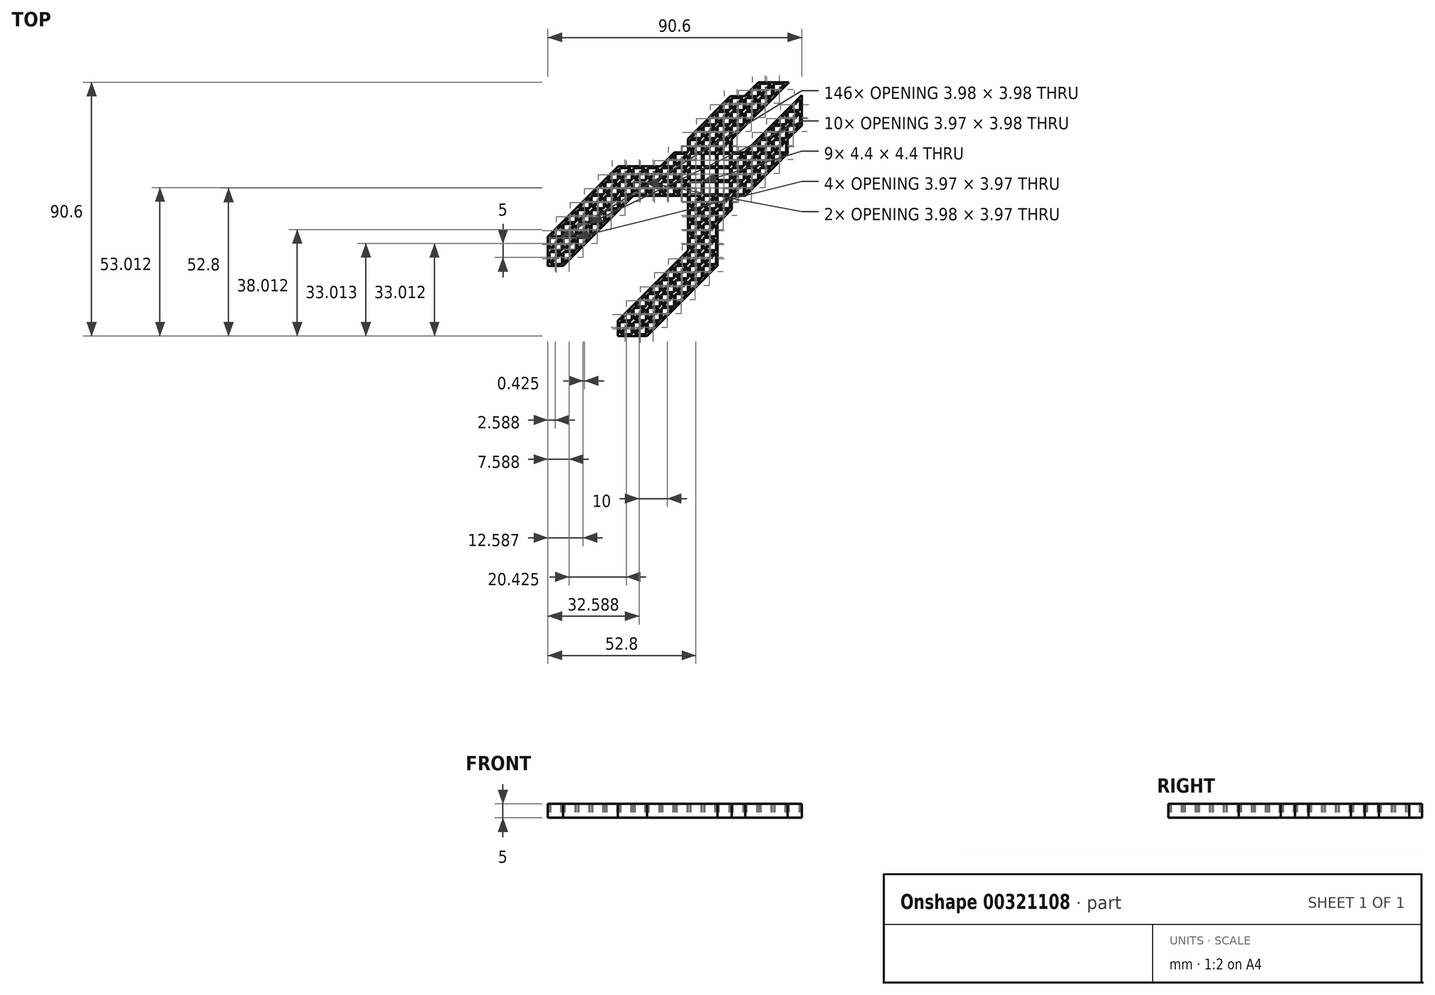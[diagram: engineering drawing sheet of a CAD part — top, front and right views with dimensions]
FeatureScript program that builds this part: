
annotation { "Feature Type Name" : "Feature", "Feature Type Description" : "" }
export const myFeature = defineFeature(function(context is Context, id is Id, definition is map)
    precondition{}
    {
        {
            var Q0;
            Q0=qCreatedBy(makeId("Top.planeOp"),FACE);
            var sketch = newSketch(context, id + "F0", { "sketchPlane" : qUnion([Q0])});
            skLineSegment(sketch, "E0", {"start": v(25.72, 10.3) * mm, "end": v(29.7, 14.28) * mm});
            skLineSegment(sketch, "E1", {"start": v(29.7, 14.28) * mm, "end": v(29.7, 10.3) * mm});
            skLineSegment(sketch, "E2", {"start": v(29.7, 10.3) * mm, "end": v(25.72, 10.3) * mm});
            skLineSegment(sketch, "E3", {"start": v(19.7, 0.3) * mm, "end": v(15.72, 0.3) * mm});
            skLineSegment(sketch, "E4", {"start": v(15.72, 0.3) * mm, "end": v(19.7, 4.28) * mm});
            skLineSegment(sketch, "E5", {"start": v(19.7, 4.28) * mm, "end": v(19.7, 0.3) * mm});
            skLineSegment(sketch, "E6", {"start": v(5.72, -24.7) * mm, "end": v(9.7, -20.72) * mm});
            skLineSegment(sketch, "E7", {"start": v(9.7, -20.72) * mm, "end": v(9.7, -24.7) * mm});
            skLineSegment(sketch, "E8", {"start": v(9.7, -24.7) * mm, "end": v(5.72, -24.7) * mm});
            skLineSegment(sketch, "E9", {"start": v(0.72, -29.7) * mm, "end": v(4.7, -25.72) * mm});
            skLineSegment(sketch, "E10", {"start": v(4.7, -25.72) * mm, "end": v(4.7, -29.7) * mm});
            skLineSegment(sketch, "E11", {"start": v(4.7, -29.7) * mm, "end": v(0.72, -29.7) * mm});
            skLineSegment(sketch, "E12", {"start": v(-4.28, -34.7) * mm, "end": v(-0.3, -30.72) * mm});
            skLineSegment(sketch, "E13", {"start": v(-0.3, -30.72) * mm, "end": v(-0.3, -34.7) * mm});
            skLineSegment(sketch, "E14", {"start": v(-0.3, -34.7) * mm, "end": v(-4.28, -34.7) * mm});
            skLineSegment(sketch, "E15", {"start": v(-9.28, -39.7) * mm, "end": v(-5.3, -35.72) * mm});
            skLineSegment(sketch, "E16", {"start": v(-5.3, -35.72) * mm, "end": v(-5.3, -39.7) * mm});
            skLineSegment(sketch, "E17", {"start": v(-5.3, -39.7) * mm, "end": v(-9.28, -39.7) * mm});
            skLineSegment(sketch, "E18", {"start": v(-19.7, -40.3) * mm, "end": v(-15.72, -40.3) * mm});
            skLineSegment(sketch, "E19", {"start": v(-15.72, -40.3) * mm, "end": v(-19.7, -44.28) * mm});
            skLineSegment(sketch, "E20", {"start": v(-19.7, -44.28) * mm, "end": v(-19.7, -40.3) * mm});
            skLineSegment(sketch, "E21", {"start": v(-24.28, 0.3) * mm, "end": v(-20.3, 4.28) * mm});
            skLineSegment(sketch, "E22", {"start": v(-20.3, 4.28) * mm, "end": v(-20.3, 0.3) * mm});
            skLineSegment(sketch, "E23", {"start": v(-20.3, 0.3) * mm, "end": v(-24.28, 0.3) * mm});
            skLineSegment(sketch, "E24", {"start": v(-29.28, -4.7) * mm, "end": v(-25.3, -0.72) * mm});
            skLineSegment(sketch, "E25", {"start": v(-25.3, -0.72) * mm, "end": v(-25.3, -4.7) * mm});
            skLineSegment(sketch, "E26", {"start": v(-25.3, -4.7) * mm, "end": v(-29.28, -4.7) * mm});
            skLineSegment(sketch, "E27", {"start": v(-39.28, -14.7) * mm, "end": v(-35.3, -10.72) * mm});
            skLineSegment(sketch, "E28", {"start": v(-35.3, -10.72) * mm, "end": v(-35.3, -14.7) * mm});
            skLineSegment(sketch, "E29", {"start": v(-35.3, -14.7) * mm, "end": v(-39.28, -14.7) * mm});
            skLineSegment(sketch, "E30", {"start": v(34.7, 40.3) * mm, "end": v(30.72, 40.3) * mm});
            skLineSegment(sketch, "E31", {"start": v(30.72, 40.3) * mm, "end": v(34.7, 44.28) * mm});
            skLineSegment(sketch, "E32", {"start": v(34.7, 44.28) * mm, "end": v(34.7, 40.3) * mm});
            skLineSegment(sketch, "E33", {"start": v(25.72, 35.3) * mm, "end": v(29.7, 39.28) * mm});
            skLineSegment(sketch, "E34", {"start": v(29.7, 39.28) * mm, "end": v(29.7, 35.3) * mm});
            skLineSegment(sketch, "E35", {"start": v(29.7, 35.3) * mm, "end": v(25.72, 35.3) * mm});
            skLineSegment(sketch, "E36", {"start": v(20.72, 30.3) * mm, "end": v(24.7, 34.28) * mm});
            skLineSegment(sketch, "E37", {"start": v(24.7, 34.28) * mm, "end": v(24.7, 30.3) * mm});
            skLineSegment(sketch, "E38", {"start": v(24.7, 30.3) * mm, "end": v(20.72, 30.3) * mm});
            skLineSegment(sketch, "E39", {"start": v(-15.3, 9.28) * mm, "end": v(-15.3, 5.3) * mm});
            skLineSegment(sketch, "E40", {"start": v(-15.3, 5.3) * mm, "end": v(-19.28, 5.3) * mm});
            skLineSegment(sketch, "E41", {"start": v(-19.28, 5.3) * mm, "end": v(-15.3, 9.28) * mm});
            skLineSegment(sketch, "E42", {"start": v(-19.7, 5.72) * mm, "end": v(-19.7, 9.7) * mm});
            skLineSegment(sketch, "E43", {"start": v(-19.7, 9.7) * mm, "end": v(-15.72, 9.7) * mm});
            skLineSegment(sketch, "E44", {"start": v(-15.72, 9.7) * mm, "end": v(-19.7, 5.72) * mm});
            skLineSegment(sketch, "E45", {"start": v(-15.3, 10.3) * mm, "end": v(-19.28, 10.3) * mm});
            skLineSegment(sketch, "E46", {"start": v(-19.28, 10.3) * mm, "end": v(-15.3, 14.28) * mm});
            skLineSegment(sketch, "E47", {"start": v(-15.3, 14.28) * mm, "end": v(-15.3, 10.3) * mm});
            skLineSegment(sketch, "E48", {"start": v(-20.3, 5.3) * mm, "end": v(-24.28, 5.3) * mm});
            skLineSegment(sketch, "E49", {"start": v(-24.28, 5.3) * mm, "end": v(-20.3, 9.28) * mm});
            skLineSegment(sketch, "E50", {"start": v(-20.3, 9.28) * mm, "end": v(-20.3, 5.3) * mm});
            skLineSegment(sketch, "E51", {"start": v(-34.28, -4.7) * mm, "end": v(-30.3, -0.72) * mm});
            skLineSegment(sketch, "E52", {"start": v(-30.3, -0.72) * mm, "end": v(-30.3, -4.7) * mm});
            skLineSegment(sketch, "E53", {"start": v(-30.3, -4.7) * mm, "end": v(-34.28, -4.7) * mm});
            skLineSegment(sketch, "E54", {"start": v(-39.28, -9.7) * mm, "end": v(-35.3, -5.72) * mm});
            skLineSegment(sketch, "E55", {"start": v(-35.3, -5.72) * mm, "end": v(-35.3, -9.7) * mm});
            skLineSegment(sketch, "E56", {"start": v(-35.3, -9.7) * mm, "end": v(-39.28, -9.7) * mm});
            skLineSegment(sketch, "E57", {"start": v(-40.3, -14.7) * mm, "end": v(-44.28, -14.7) * mm});
            skLineSegment(sketch, "E58", {"start": v(-44.28, -14.7) * mm, "end": v(-40.3, -10.72) * mm});
            skLineSegment(sketch, "E59", {"start": v(-40.3, -10.72) * mm, "end": v(-40.3, -14.7) * mm});
            skLineSegment(sketch, "E60", {"start": v(-39.7, -10.3) * mm, "end": v(-35.72, -10.3) * mm});
            skLineSegment(sketch, "E61", {"start": v(-35.72, -10.3) * mm, "end": v(-39.7, -14.27) * mm});
            skLineSegment(sketch, "E62", {"start": v(-39.7, -14.27) * mm, "end": v(-39.7, -10.3) * mm});
            skLineSegment(sketch, "E63", {"start": v(-34.7, -5.3) * mm, "end": v(-30.72, -5.3) * mm});
            skLineSegment(sketch, "E64", {"start": v(-30.72, -5.3) * mm, "end": v(-34.7, -9.28) * mm});
            skLineSegment(sketch, "E65", {"start": v(-34.7, -9.28) * mm, "end": v(-34.7, -5.3) * mm});
            skLineSegment(sketch, "E66", {"start": v(-29.7, -0.3) * mm, "end": v(-25.72, -0.3) * mm});
            skLineSegment(sketch, "E67", {"start": v(-25.72, -0.3) * mm, "end": v(-29.7, -4.28) * mm});
            skLineSegment(sketch, "E68", {"start": v(-29.7, -4.28) * mm, "end": v(-29.7, -0.3) * mm});
            skLineSegment(sketch, "E69", {"start": v(-29.28, 0.3) * mm, "end": v(-25.3, 4.28) * mm});
            skLineSegment(sketch, "E70", {"start": v(-25.3, 4.28) * mm, "end": v(-25.3, 0.3) * mm});
            skLineSegment(sketch, "E71", {"start": v(-25.3, 0.3) * mm, "end": v(-29.28, 0.3) * mm});
            skLineSegment(sketch, "E72", {"start": v(-24.7, 4.7) * mm, "end": v(-20.72, 4.7) * mm});
            skLineSegment(sketch, "E73", {"start": v(-20.72, 4.7) * mm, "end": v(-24.7, 0.72) * mm});
            skLineSegment(sketch, "E74", {"start": v(-24.7, 0.72) * mm, "end": v(-24.7, 4.7) * mm});
            skLineSegment(sketch, "E75", {"start": v(-14.7, 9.7) * mm, "end": v(-10.72, 9.7) * mm});
            skLineSegment(sketch, "E76", {"start": v(-10.72, 9.7) * mm, "end": v(-14.7, 5.72) * mm});
            skLineSegment(sketch, "E77", {"start": v(-14.7, 5.72) * mm, "end": v(-14.7, 9.7) * mm});
            skLineSegment(sketch, "E78", {"start": v(34.7, 19.28) * mm, "end": v(34.7, 15.3) * mm});
            skLineSegment(sketch, "E79", {"start": v(34.7, 15.3) * mm, "end": v(30.72, 15.3) * mm});
            skLineSegment(sketch, "E80", {"start": v(30.72, 15.3) * mm, "end": v(34.7, 19.28) * mm});
            skLineSegment(sketch, "E81", {"start": v(30.3, 15.72) * mm, "end": v(30.3, 19.7) * mm});
            skLineSegment(sketch, "E82", {"start": v(30.3, 19.7) * mm, "end": v(34.28, 19.7) * mm});
            skLineSegment(sketch, "E83", {"start": v(34.28, 19.7) * mm, "end": v(30.3, 15.72) * mm});
            skLineSegment(sketch, "E84", {"start": v(30.72, 20.3) * mm, "end": v(34.7, 24.28) * mm});
            skLineSegment(sketch, "E85", {"start": v(34.7, 24.28) * mm, "end": v(34.7, 20.3) * mm});
            skLineSegment(sketch, "E86", {"start": v(34.7, 20.3) * mm, "end": v(30.72, 20.3) * mm});
            skLineSegment(sketch, "E87", {"start": v(29.7, 15.3) * mm, "end": v(25.72, 15.3) * mm});
            skLineSegment(sketch, "E88", {"start": v(25.72, 15.3) * mm, "end": v(29.7, 19.28) * mm});
            skLineSegment(sketch, "E89", {"start": v(29.7, 19.28) * mm, "end": v(29.7, 15.3) * mm});
            skLineSegment(sketch, "E90", {"start": v(5.3, 19.7) * mm, "end": v(9.7, 19.7) * mm});
            skLineSegment(sketch, "E91", {"start": v(9.7, 19.7) * mm, "end": v(9.7, 15.3) * mm});
            skLineSegment(sketch, "E92", {"start": v(9.7, 15.3) * mm, "end": v(5.3, 15.3) * mm});
            skLineSegment(sketch, "E93", {"start": v(5.3, 15.3) * mm, "end": v(5.3, 19.7) * mm});
            skLineSegment(sketch, "E94", {"start": v(20.3, 14.7) * mm, "end": v(24.28, 14.7) * mm});
            skLineSegment(sketch, "E95", {"start": v(24.28, 14.7) * mm, "end": v(20.3, 10.72) * mm});
            skLineSegment(sketch, "E96", {"start": v(20.3, 10.72) * mm, "end": v(20.3, 14.7) * mm});
            skLineSegment(sketch, "E97", {"start": v(19.7, 10.3) * mm, "end": v(15.3, 10.3) * mm});
            skLineSegment(sketch, "E98", {"start": v(15.3, 10.3) * mm, "end": v(15.3, 14.7) * mm});
            skLineSegment(sketch, "E99", {"start": v(15.3, 14.7) * mm, "end": v(19.7, 14.7) * mm});
            skLineSegment(sketch, "E100", {"start": v(19.7, 14.7) * mm, "end": v(19.7, 10.3) * mm});
            skLineSegment(sketch, "E101", {"start": v(10.3, 14.7) * mm, "end": v(14.7, 14.7) * mm});
            skLineSegment(sketch, "E102", {"start": v(14.7, 14.7) * mm, "end": v(14.7, 10.3) * mm});
            skLineSegment(sketch, "E103", {"start": v(14.7, 10.3) * mm, "end": v(10.3, 10.3) * mm});
            skLineSegment(sketch, "E104", {"start": v(10.3, 10.3) * mm, "end": v(10.3, 14.7) * mm});
            skLineSegment(sketch, "E105", {"start": v(14.7, 15.3) * mm, "end": v(10.3, 15.3) * mm});
            skLineSegment(sketch, "E106", {"start": v(10.3, 15.3) * mm, "end": v(10.3, 19.7) * mm});
            skLineSegment(sketch, "E107", {"start": v(10.3, 19.7) * mm, "end": v(14.7, 19.7) * mm});
            skLineSegment(sketch, "E108", {"start": v(14.7, 19.7) * mm, "end": v(14.7, 15.3) * mm});
            skLineSegment(sketch, "E109", {"start": v(14.7, 9.7) * mm, "end": v(14.7, 5.3) * mm});
            skLineSegment(sketch, "E110", {"start": v(14.7, 5.3) * mm, "end": v(10.3, 5.3) * mm});
            skLineSegment(sketch, "E111", {"start": v(10.3, 5.3) * mm, "end": v(10.3, 9.7) * mm});
            skLineSegment(sketch, "E112", {"start": v(10.3, 9.7) * mm, "end": v(14.7, 9.7) * mm});
            skLineSegment(sketch, "E113", {"start": v(10.72, 20.3) * mm, "end": v(14.7, 24.28) * mm});
            skLineSegment(sketch, "E114", {"start": v(14.7, 24.28) * mm, "end": v(14.7, 20.3) * mm});
            skLineSegment(sketch, "E115", {"start": v(14.7, 20.3) * mm, "end": v(10.72, 20.3) * mm});
            skLineSegment(sketch, "E116", {"start": v(10.72, 25.3) * mm, "end": v(14.7, 29.28) * mm});
            skLineSegment(sketch, "E117", {"start": v(14.7, 29.28) * mm, "end": v(14.7, 25.3) * mm});
            skLineSegment(sketch, "E118", {"start": v(14.7, 25.3) * mm, "end": v(10.72, 25.3) * mm});
            skLineSegment(sketch, "E119", {"start": v(15.3, 29.7) * mm, "end": v(19.28, 29.7) * mm});
            skLineSegment(sketch, "E120", {"start": v(19.28, 29.7) * mm, "end": v(15.3, 25.72) * mm});
            skLineSegment(sketch, "E121", {"start": v(15.3, 25.72) * mm, "end": v(15.3, 29.7) * mm});
            skLineSegment(sketch, "E122", {"start": v(10.3, 25.73) * mm, "end": v(10.3, 29.7) * mm});
            skLineSegment(sketch, "E123", {"start": v(10.3, 29.7) * mm, "end": v(14.28, 29.7) * mm});
            skLineSegment(sketch, "E124", {"start": v(14.28, 29.7) * mm, "end": v(10.3, 25.73) * mm});
            skLineSegment(sketch, "E125", {"start": v(14.28, 24.7) * mm, "end": v(10.3, 20.72) * mm});
            skLineSegment(sketch, "E126", {"start": v(10.3, 20.72) * mm, "end": v(10.3, 24.7) * mm});
            skLineSegment(sketch, "E127", {"start": v(10.3, 24.7) * mm, "end": v(14.28, 24.7) * mm});
            skLineSegment(sketch, "E128", {"start": v(5.3, 14.7) * mm, "end": v(9.7, 14.7) * mm});
            skLineSegment(sketch, "E129", {"start": v(9.7, 14.7) * mm, "end": v(9.7, 10.3) * mm});
            skLineSegment(sketch, "E130", {"start": v(9.7, 10.3) * mm, "end": v(5.3, 10.3) * mm});
            skLineSegment(sketch, "E131", {"start": v(5.3, 10.3) * mm, "end": v(5.3, 14.7) * mm});
            skLineSegment(sketch, "E132", {"start": v(14.28, 4.7) * mm, "end": v(10.3, 0.72) * mm});
            skLineSegment(sketch, "E133", {"start": v(10.3, 0.72) * mm, "end": v(10.3, 4.7) * mm});
            skLineSegment(sketch, "E134", {"start": v(10.3, 4.7) * mm, "end": v(14.28, 4.7) * mm});
            skLineSegment(sketch, "E135", {"start": v(5.72, -4.7) * mm, "end": v(9.7, -0.72) * mm});
            skLineSegment(sketch, "E136", {"start": v(9.7, -0.72) * mm, "end": v(9.7, -4.7) * mm});
            skLineSegment(sketch, "E137", {"start": v(9.7, -4.7) * mm, "end": v(5.72, -4.7) * mm});
            skLineSegment(sketch, "E138", {"start": v(5.72, -9.7) * mm, "end": v(9.7, -5.72) * mm});
            skLineSegment(sketch, "E139", {"start": v(9.7, -5.72) * mm, "end": v(9.7, -9.7) * mm});
            skLineSegment(sketch, "E140", {"start": v(9.7, -9.7) * mm, "end": v(5.72, -9.7) * mm});
            skLineSegment(sketch, "E141", {"start": v(14.28, -10.3) * mm, "end": v(10.3, -14.28) * mm});
            skLineSegment(sketch, "E142", {"start": v(10.3, -14.28) * mm, "end": v(10.3, -10.3) * mm});
            skLineSegment(sketch, "E143", {"start": v(10.3, -10.3) * mm, "end": v(14.28, -10.3) * mm});
            skLineSegment(sketch, "E144", {"start": v(10.3, -5.3) * mm, "end": v(14.28, -5.3) * mm});
            skLineSegment(sketch, "E145", {"start": v(14.28, -5.3) * mm, "end": v(10.3, -9.28) * mm});
            skLineSegment(sketch, "E146", {"start": v(10.3, -9.28) * mm, "end": v(10.3, -5.3) * mm});
            skLineSegment(sketch, "E147", {"start": v(10.3, -0.3) * mm, "end": v(14.28, -0.3) * mm});
            skLineSegment(sketch, "E148", {"start": v(14.28, -0.3) * mm, "end": v(10.3, -4.28) * mm});
            skLineSegment(sketch, "E149", {"start": v(10.3, -4.28) * mm, "end": v(10.3, -0.3) * mm});
            skLineSegment(sketch, "E150", {"start": v(10.72, 0.3) * mm, "end": v(14.7, 4.28) * mm});
            skLineSegment(sketch, "E151", {"start": v(14.7, 4.28) * mm, "end": v(14.7, 0.3) * mm});
            skLineSegment(sketch, "E152", {"start": v(14.7, 0.3) * mm, "end": v(10.72, 0.3) * mm});
            skLineSegment(sketch, "E153", {"start": v(19.7, 5.3) * mm, "end": v(15.3, 5.3) * mm});
            skLineSegment(sketch, "E154", {"start": v(15.3, 5.3) * mm, "end": v(15.3, 9.7) * mm});
            skLineSegment(sketch, "E155", {"start": v(15.3, 9.7) * mm, "end": v(19.7, 9.7) * mm});
            skLineSegment(sketch, "E156", {"start": v(19.7, 9.7) * mm, "end": v(19.7, 5.3) * mm});
            skLineSegment(sketch, "E157", {"start": v(20.72, 10.3) * mm, "end": v(24.7, 14.28) * mm});
            skLineSegment(sketch, "E158", {"start": v(24.7, 14.28) * mm, "end": v(24.7, 10.3) * mm});
            skLineSegment(sketch, "E159", {"start": v(24.7, 10.3) * mm, "end": v(20.72, 10.3) * mm});
            skLineSegment(sketch, "E160", {"start": v(20.72, 15.3) * mm, "end": v(24.7, 19.28) * mm});
            skLineSegment(sketch, "E161", {"start": v(24.7, 19.28) * mm, "end": v(24.7, 15.3) * mm});
            skLineSegment(sketch, "E162", {"start": v(24.7, 15.3) * mm, "end": v(20.72, 15.3) * mm});
            skLineSegment(sketch, "E163", {"start": v(19.7, 15.3) * mm, "end": v(15.3, 15.3) * mm});
            skLineSegment(sketch, "E164", {"start": v(15.3, 15.3) * mm, "end": v(15.3, 19.7) * mm});
            skLineSegment(sketch, "E165", {"start": v(15.3, 19.7) * mm, "end": v(19.7, 19.7) * mm});
            skLineSegment(sketch, "E166", {"start": v(19.7, 19.7) * mm, "end": v(19.7, 15.3) * mm});
            skLineSegment(sketch, "E167", {"start": v(15.3, 24.7) * mm, "end": v(19.28, 24.7) * mm});
            skLineSegment(sketch, "E168", {"start": v(19.28, 24.7) * mm, "end": v(15.3, 20.72) * mm});
            skLineSegment(sketch, "E169", {"start": v(15.3, 20.72) * mm, "end": v(15.3, 24.7) * mm});
            skLineSegment(sketch, "E170", {"start": v(19.7, 25.3) * mm, "end": v(15.72, 25.3) * mm});
            skLineSegment(sketch, "E171", {"start": v(15.72, 25.3) * mm, "end": v(19.7, 29.28) * mm});
            skLineSegment(sketch, "E172", {"start": v(19.7, 29.28) * mm, "end": v(19.7, 25.3) * mm});
            skLineSegment(sketch, "E173", {"start": v(20.72, 35.3) * mm, "end": v(24.7, 39.28) * mm});
            skLineSegment(sketch, "E174", {"start": v(24.7, 39.28) * mm, "end": v(24.7, 35.3) * mm});
            skLineSegment(sketch, "E175", {"start": v(24.7, 35.3) * mm, "end": v(20.72, 35.3) * mm});
            skLineSegment(sketch, "E176", {"start": v(24.28, 34.7) * mm, "end": v(20.3, 30.72) * mm});
            skLineSegment(sketch, "E177", {"start": v(20.3, 30.72) * mm, "end": v(20.3, 34.7) * mm});
            skLineSegment(sketch, "E178", {"start": v(20.3, 34.7) * mm, "end": v(24.28, 34.7) * mm});
            skLineSegment(sketch, "E179", {"start": v(19.7, 30.3) * mm, "end": v(15.72, 30.3) * mm});
            skLineSegment(sketch, "E180", {"start": v(15.72, 30.3) * mm, "end": v(19.7, 34.28) * mm});
            skLineSegment(sketch, "E181", {"start": v(19.7, 34.28) * mm, "end": v(19.7, 30.3) * mm});
            skLineSegment(sketch, "E182", {"start": v(9.7, 20.3) * mm, "end": v(5.72, 20.3) * mm});
            skLineSegment(sketch, "E183", {"start": v(5.72, 20.3) * mm, "end": v(9.7, 24.28) * mm});
            skLineSegment(sketch, "E184", {"start": v(9.7, 24.28) * mm, "end": v(9.7, 20.3) * mm});
            skLineSegment(sketch, "E185", {"start": v(4.7, 15.3) * mm, "end": v(0.72, 15.3) * mm});
            skLineSegment(sketch, "E186", {"start": v(0.72, 15.3) * mm, "end": v(4.7, 19.28) * mm});
            skLineSegment(sketch, "E187", {"start": v(4.7, 19.28) * mm, "end": v(4.7, 15.3) * mm});
            skLineSegment(sketch, "E188", {"start": v(4.28, 14.7) * mm, "end": v(0.3, 10.72) * mm});
            skLineSegment(sketch, "E189", {"start": v(0.3, 10.72) * mm, "end": v(0.3, 14.7) * mm});
            skLineSegment(sketch, "E190", {"start": v(0.3, 14.7) * mm, "end": v(4.28, 14.7) * mm});
            skLineSegment(sketch, "E191", {"start": v(-0.3, 10.3) * mm, "end": v(-4.28, 10.3) * mm});
            skLineSegment(sketch, "E192", {"start": v(-4.28, 10.3) * mm, "end": v(-0.3, 14.28) * mm});
            skLineSegment(sketch, "E193", {"start": v(-0.3, 14.28) * mm, "end": v(-0.3, 10.3) * mm});
            skLineSegment(sketch, "E194", {"start": v(-5.3, 10.3) * mm, "end": v(-9.28, 10.3) * mm});
            skLineSegment(sketch, "E195", {"start": v(-9.28, 10.3) * mm, "end": v(-5.3, 14.28) * mm});
            skLineSegment(sketch, "E196", {"start": v(-5.3, 14.28) * mm, "end": v(-5.3, 10.3) * mm});
            skLineSegment(sketch, "E197", {"start": v(-4.7, 9.7) * mm, "end": v(-0.72, 9.7) * mm});
            skLineSegment(sketch, "E198", {"start": v(-0.72, 9.7) * mm, "end": v(-4.7, 5.72) * mm});
            skLineSegment(sketch, "E199", {"start": v(-4.7, 5.72) * mm, "end": v(-4.7, 9.7) * mm});
            skLineSegment(sketch, "E200", {"start": v(4.7, 14.28) * mm, "end": v(4.7, 10.3) * mm});
            skLineSegment(sketch, "E201", {"start": v(4.7, 10.3) * mm, "end": v(0.72, 10.3) * mm});
            skLineSegment(sketch, "E202", {"start": v(0.72, 10.3) * mm, "end": v(4.7, 14.28) * mm});
            skLineSegment(sketch, "E203", {"start": v(5.3, 9.7) * mm, "end": v(9.7, 9.7) * mm});
            skLineSegment(sketch, "E204", {"start": v(9.7, 9.7) * mm, "end": v(9.7, 5.3) * mm});
            skLineSegment(sketch, "E205", {"start": v(9.7, 5.3) * mm, "end": v(5.3, 5.3) * mm});
            skLineSegment(sketch, "E206", {"start": v(5.3, 5.3) * mm, "end": v(5.3, 9.7) * mm});
            skLineSegment(sketch, "E207", {"start": v(9.7, 0.3) * mm, "end": v(5.72, 0.3) * mm});
            skLineSegment(sketch, "E208", {"start": v(5.72, 0.3) * mm, "end": v(9.7, 4.28) * mm});
            skLineSegment(sketch, "E209", {"start": v(9.7, 4.28) * mm, "end": v(9.7, 0.3) * mm});
            skLineSegment(sketch, "E210", {"start": v(5.3, -0.3) * mm, "end": v(9.28, -0.3) * mm});
            skLineSegment(sketch, "E211", {"start": v(9.28, -0.3) * mm, "end": v(5.3, -4.28) * mm});
            skLineSegment(sketch, "E212", {"start": v(5.3, -4.28) * mm, "end": v(5.3, -0.3) * mm});
            skLineSegment(sketch, "E213", {"start": v(5.3, -5.3) * mm, "end": v(9.27, -5.3) * mm});
            skLineSegment(sketch, "E214", {"start": v(9.27, -5.3) * mm, "end": v(5.3, -9.28) * mm});
            skLineSegment(sketch, "E215", {"start": v(5.3, -9.28) * mm, "end": v(5.3, -5.3) * mm});
            skLineSegment(sketch, "E216", {"start": v(9.7, -14.7) * mm, "end": v(5.72, -14.7) * mm});
            skLineSegment(sketch, "E217", {"start": v(5.72, -14.7) * mm, "end": v(9.7, -10.72) * mm});
            skLineSegment(sketch, "E218", {"start": v(9.7, -10.72) * mm, "end": v(9.7, -14.7) * mm});
            skLineSegment(sketch, "E219", {"start": v(5.3, -15.3) * mm, "end": v(9.28, -15.3) * mm});
            skLineSegment(sketch, "E220", {"start": v(9.28, -15.3) * mm, "end": v(5.3, -19.28) * mm});
            skLineSegment(sketch, "E221", {"start": v(5.3, -19.28) * mm, "end": v(5.3, -15.3) * mm});
            skLineSegment(sketch, "E222", {"start": v(9.7, -15.72) * mm, "end": v(9.7, -19.7) * mm});
            skLineSegment(sketch, "E223", {"start": v(9.7, -19.7) * mm, "end": v(5.72, -19.7) * mm});
            skLineSegment(sketch, "E224", {"start": v(5.72, -19.7) * mm, "end": v(9.7, -15.72) * mm});
            skLineSegment(sketch, "E225", {"start": v(-14.28, -39.7) * mm, "end": v(-10.3, -35.72) * mm});
            skLineSegment(sketch, "E226", {"start": v(-10.3, -35.72) * mm, "end": v(-10.3, -39.7) * mm});
            skLineSegment(sketch, "E227", {"start": v(-10.3, -39.7) * mm, "end": v(-14.28, -39.7) * mm});
            skLineSegment(sketch, "E228", {"start": v(-9.7, -35.3) * mm, "end": v(-5.72, -35.3) * mm});
            skLineSegment(sketch, "E229", {"start": v(-5.72, -35.3) * mm, "end": v(-9.7, -39.28) * mm});
            skLineSegment(sketch, "E230", {"start": v(-9.7, -39.28) * mm, "end": v(-9.7, -35.3) * mm});
            skLineSegment(sketch, "E231", {"start": v(-9.28, -34.7) * mm, "end": v(-5.3, -30.72) * mm});
            skLineSegment(sketch, "E232", {"start": v(-5.3, -30.72) * mm, "end": v(-5.3, -34.7) * mm});
            skLineSegment(sketch, "E233", {"start": v(-5.3, -34.7) * mm, "end": v(-9.28, -34.7) * mm});
            skLineSegment(sketch, "E234", {"start": v(-4.7, -30.3) * mm, "end": v(-0.72, -30.3) * mm});
            skLineSegment(sketch, "E235", {"start": v(-0.72, -30.3) * mm, "end": v(-4.7, -34.28) * mm});
            skLineSegment(sketch, "E236", {"start": v(-4.7, -34.28) * mm, "end": v(-4.7, -30.3) * mm});
            skLineSegment(sketch, "E237", {"start": v(-4.28, -29.7) * mm, "end": v(-0.3, -25.72) * mm});
            skLineSegment(sketch, "E238", {"start": v(-0.3, -25.72) * mm, "end": v(-0.3, -29.7) * mm});
            skLineSegment(sketch, "E239", {"start": v(-0.3, -29.7) * mm, "end": v(-4.28, -29.7) * mm});
            skLineSegment(sketch, "E240", {"start": v(0.3, -25.3) * mm, "end": v(4.28, -25.3) * mm});
            skLineSegment(sketch, "E241", {"start": v(4.28, -25.3) * mm, "end": v(0.3, -29.28) * mm});
            skLineSegment(sketch, "E242", {"start": v(0.3, -29.28) * mm, "end": v(0.3, -25.3) * mm});
            skLineSegment(sketch, "E243", {"start": v(0.72, -24.7) * mm, "end": v(4.7, -20.72) * mm});
            skLineSegment(sketch, "E244", {"start": v(4.7, -20.72) * mm, "end": v(4.7, -24.7) * mm});
            skLineSegment(sketch, "E245", {"start": v(4.7, -24.7) * mm, "end": v(0.72, -24.7) * mm});
            skLineSegment(sketch, "E246", {"start": v(5.3, -20.3) * mm, "end": v(9.28, -20.3) * mm});
            skLineSegment(sketch, "E247", {"start": v(9.28, -20.3) * mm, "end": v(5.3, -24.28) * mm});
            skLineSegment(sketch, "E248", {"start": v(5.3, -24.28) * mm, "end": v(5.3, -20.3) * mm});
            skLineSegment(sketch, "E249", {"start": v(10.3, -15.3) * mm, "end": v(14.28, -15.3) * mm});
            skLineSegment(sketch, "E250", {"start": v(14.28, -15.3) * mm, "end": v(10.3, -19.28) * mm});
            skLineSegment(sketch, "E251", {"start": v(10.3, -19.28) * mm, "end": v(10.3, -15.3) * mm});
            skLineSegment(sketch, "E252", {"start": v(14.7, -14.7) * mm, "end": v(10.72, -14.7) * mm});
            skLineSegment(sketch, "E253", {"start": v(10.72, -14.7) * mm, "end": v(14.7, -10.72) * mm});
            skLineSegment(sketch, "E254", {"start": v(14.7, -10.72) * mm, "end": v(14.7, -14.7) * mm});
            skLineSegment(sketch, "E255", {"start": v(14.7, -9.7) * mm, "end": v(10.72, -9.7) * mm});
            skLineSegment(sketch, "E256", {"start": v(10.72, -9.7) * mm, "end": v(14.7, -5.72) * mm});
            skLineSegment(sketch, "E257", {"start": v(14.7, -5.72) * mm, "end": v(14.7, -9.7) * mm});
            skLineSegment(sketch, "E258", {"start": v(14.7, -4.7) * mm, "end": v(10.72, -4.7) * mm});
            skLineSegment(sketch, "E259", {"start": v(10.72, -4.7) * mm, "end": v(14.7, -0.72) * mm});
            skLineSegment(sketch, "E260", {"start": v(14.7, -0.72) * mm, "end": v(14.7, -4.7) * mm});
            skLineSegment(sketch, "E261", {"start": v(15.3, 4.7) * mm, "end": v(19.28, 4.7) * mm});
            skLineSegment(sketch, "E262", {"start": v(19.28, 4.7) * mm, "end": v(15.3, 0.72) * mm});
            skLineSegment(sketch, "E263", {"start": v(15.3, 0.72) * mm, "end": v(15.3, 4.7) * mm});
            skLineSegment(sketch, "E264", {"start": v(25.3, 14.7) * mm, "end": v(29.28, 14.7) * mm});
            skLineSegment(sketch, "E265", {"start": v(29.28, 14.7) * mm, "end": v(25.3, 10.72) * mm});
            skLineSegment(sketch, "E266", {"start": v(25.3, 10.72) * mm, "end": v(25.3, 14.7) * mm});
            skLineSegment(sketch, "E267", {"start": v(35.3, 24.7) * mm, "end": v(39.28, 24.7) * mm});
            skLineSegment(sketch, "E268", {"start": v(39.28, 24.7) * mm, "end": v(35.3, 20.72) * mm});
            skLineSegment(sketch, "E269", {"start": v(35.3, 20.72) * mm, "end": v(35.3, 24.7) * mm});
            skLineSegment(sketch, "E270", {"start": v(39.7, 25.3) * mm, "end": v(35.72, 25.3) * mm});
            skLineSegment(sketch, "E271", {"start": v(35.72, 25.3) * mm, "end": v(39.7, 29.28) * mm});
            skLineSegment(sketch, "E272", {"start": v(39.7, 29.28) * mm, "end": v(39.7, 25.3) * mm});
            skLineSegment(sketch, "E273", {"start": v(44.28, 34.7) * mm, "end": v(40.3, 30.72) * mm});
            skLineSegment(sketch, "E274", {"start": v(40.3, 30.72) * mm, "end": v(40.3, 34.7) * mm});
            skLineSegment(sketch, "E275", {"start": v(40.3, 34.7) * mm, "end": v(44.28, 34.7) * mm});
            skLineSegment(sketch, "E276", {"start": v(35.3, 25.72) * mm, "end": v(35.3, 29.7) * mm});
            skLineSegment(sketch, "E277", {"start": v(35.3, 29.7) * mm, "end": v(39.28, 29.7) * mm});
            skLineSegment(sketch, "E278", {"start": v(39.28, 29.7) * mm, "end": v(35.3, 25.72) * mm});
            skLineSegment(sketch, "E279", {"start": v(30.3, 20.72) * mm, "end": v(30.3, 24.7) * mm});
            skLineSegment(sketch, "E280", {"start": v(30.3, 24.7) * mm, "end": v(34.28, 24.7) * mm});
            skLineSegment(sketch, "E281", {"start": v(34.28, 24.7) * mm, "end": v(30.3, 20.72) * mm});
            skLineSegment(sketch, "E282", {"start": v(25.3, 15.72) * mm, "end": v(25.3, 19.7) * mm});
            skLineSegment(sketch, "E283", {"start": v(25.3, 19.7) * mm, "end": v(29.28, 19.7) * mm});
            skLineSegment(sketch, "E284", {"start": v(29.28, 19.7) * mm, "end": v(25.3, 15.72) * mm});
            skLineSegment(sketch, "E285", {"start": v(20.3, 15.72) * mm, "end": v(20.3, 19.7) * mm});
            skLineSegment(sketch, "E286", {"start": v(20.3, 19.7) * mm, "end": v(24.28, 19.7) * mm});
            skLineSegment(sketch, "E287", {"start": v(24.28, 19.7) * mm, "end": v(20.3, 15.72) * mm});
            skLineSegment(sketch, "E288", {"start": v(15.72, 20.3) * mm, "end": v(19.7, 24.28) * mm});
            skLineSegment(sketch, "E289", {"start": v(19.7, 24.28) * mm, "end": v(19.7, 20.3) * mm});
            skLineSegment(sketch, "E290", {"start": v(19.7, 20.3) * mm, "end": v(15.72, 20.3) * mm});
            skLineSegment(sketch, "E291", {"start": v(30.3, 40.72) * mm, "end": v(30.3, 44.7) * mm});
            skLineSegment(sketch, "E292", {"start": v(30.3, 44.7) * mm, "end": v(34.28, 44.7) * mm});
            skLineSegment(sketch, "E293", {"start": v(34.28, 44.7) * mm, "end": v(30.3, 40.72) * mm});
            skLineSegment(sketch, "E294", {"start": v(25.3, 35.72) * mm, "end": v(25.3, 39.7) * mm});
            skLineSegment(sketch, "E295", {"start": v(25.3, 39.7) * mm, "end": v(29.28, 39.7) * mm});
            skLineSegment(sketch, "E296", {"start": v(29.28, 39.7) * mm, "end": v(25.3, 35.72) * mm});
            skLineSegment(sketch, "E297", {"start": v(20.3, 35.72) * mm, "end": v(20.3, 39.7) * mm});
            skLineSegment(sketch, "E298", {"start": v(20.3, 39.7) * mm, "end": v(24.28, 39.7) * mm});
            skLineSegment(sketch, "E299", {"start": v(24.28, 39.7) * mm, "end": v(20.3, 35.72) * mm});
            skLineSegment(sketch, "E300", {"start": v(15.3, 30.72) * mm, "end": v(15.3, 34.7) * mm});
            skLineSegment(sketch, "E301", {"start": v(15.3, 34.7) * mm, "end": v(19.28, 34.7) * mm});
            skLineSegment(sketch, "E302", {"start": v(19.28, 34.7) * mm, "end": v(15.3, 30.72) * mm});
            skLineSegment(sketch, "E303", {"start": v(9.7, 25.3) * mm, "end": v(5.73, 25.3) * mm});
            skLineSegment(sketch, "E304", {"start": v(5.73, 25.3) * mm, "end": v(9.7, 29.28) * mm});
            skLineSegment(sketch, "E305", {"start": v(9.7, 29.28) * mm, "end": v(9.7, 25.3) * mm});
            skLineSegment(sketch, "E306", {"start": v(5.3, 24.7) * mm, "end": v(9.27, 24.7) * mm});
            skLineSegment(sketch, "E307", {"start": v(9.27, 24.7) * mm, "end": v(5.3, 20.72) * mm});
            skLineSegment(sketch, "E308", {"start": v(5.3, 20.72) * mm, "end": v(5.3, 24.7) * mm});
            skLineSegment(sketch, "E309", {"start": v(0.3, 15.72) * mm, "end": v(0.3, 19.7) * mm});
            skLineSegment(sketch, "E310", {"start": v(0.3, 19.7) * mm, "end": v(4.28, 19.7) * mm});
            skLineSegment(sketch, "E311", {"start": v(4.28, 19.7) * mm, "end": v(0.3, 15.72) * mm});
            skLineSegment(sketch, "E312", {"start": v(-4.7, 10.72) * mm, "end": v(-4.7, 14.7) * mm});
            skLineSegment(sketch, "E313", {"start": v(-4.7, 14.7) * mm, "end": v(-0.72, 14.7) * mm});
            skLineSegment(sketch, "E314", {"start": v(-0.72, 14.7) * mm, "end": v(-4.7, 10.72) * mm});
            skLineSegment(sketch, "E315", {"start": v(-9.7, 10.72) * mm, "end": v(-9.7, 14.7) * mm});
            skLineSegment(sketch, "E316", {"start": v(-9.7, 14.7) * mm, "end": v(-5.72, 14.7) * mm});
            skLineSegment(sketch, "E317", {"start": v(-5.72, 14.7) * mm, "end": v(-9.7, 10.72) * mm});
            skLineSegment(sketch, "E318", {"start": v(-10.3, 10.3) * mm, "end": v(-14.28, 10.3) * mm});
            skLineSegment(sketch, "E319", {"start": v(-14.28, 10.3) * mm, "end": v(-10.3, 14.28) * mm});
            skLineSegment(sketch, "E320", {"start": v(-10.3, 14.28) * mm, "end": v(-10.3, 10.3) * mm});
            skLineSegment(sketch, "E321", {"start": v(-14.7, 10.72) * mm, "end": v(-14.7, 14.7) * mm});
            skLineSegment(sketch, "E322", {"start": v(-14.7, 14.7) * mm, "end": v(-10.72, 14.7) * mm});
            skLineSegment(sketch, "E323", {"start": v(-10.72, 14.7) * mm, "end": v(-14.7, 10.72) * mm});
            skLineSegment(sketch, "E324", {"start": v(-19.7, 10.72) * mm, "end": v(-19.7, 14.7) * mm});
            skLineSegment(sketch, "E325", {"start": v(-19.7, 14.7) * mm, "end": v(-15.72, 14.7) * mm});
            skLineSegment(sketch, "E326", {"start": v(-15.72, 14.7) * mm, "end": v(-19.7, 10.72) * mm});
            skLineSegment(sketch, "E327", {"start": v(-24.7, 5.72) * mm, "end": v(-24.7, 9.7) * mm});
            skLineSegment(sketch, "E328", {"start": v(-24.7, 9.7) * mm, "end": v(-20.72, 9.7) * mm});
            skLineSegment(sketch, "E329", {"start": v(-20.72, 9.7) * mm, "end": v(-24.7, 5.72) * mm});
            skLineSegment(sketch, "E330", {"start": v(-29.7, 0.72) * mm, "end": v(-29.7, 4.7) * mm});
            skLineSegment(sketch, "E331", {"start": v(-29.7, 4.7) * mm, "end": v(-25.72, 4.7) * mm});
            skLineSegment(sketch, "E332", {"start": v(-25.72, 4.7) * mm, "end": v(-29.7, 0.72) * mm});
            skLineSegment(sketch, "E333", {"start": v(-34.7, -4.28) * mm, "end": v(-34.7, -0.3) * mm});
            skLineSegment(sketch, "E334", {"start": v(-34.7, -0.3) * mm, "end": v(-30.72, -0.3) * mm});
            skLineSegment(sketch, "E335", {"start": v(-30.72, -0.3) * mm, "end": v(-34.7, -4.28) * mm});
            skLineSegment(sketch, "E336", {"start": v(-39.7, -9.28) * mm, "end": v(-39.7, -5.3) * mm});
            skLineSegment(sketch, "E337", {"start": v(-39.7, -5.3) * mm, "end": v(-35.72, -5.3) * mm});
            skLineSegment(sketch, "E338", {"start": v(-35.72, -5.3) * mm, "end": v(-39.7, -9.28) * mm});
            skLineSegment(sketch, "E339", {"start": v(-40.72, -10.3) * mm, "end": v(-44.7, -14.28) * mm});
            skLineSegment(sketch, "E340", {"start": v(-44.7, -14.28) * mm, "end": v(-44.7, -10.3) * mm});
            skLineSegment(sketch, "E341", {"start": v(-44.7, -10.3) * mm, "end": v(-40.72, -10.3) * mm});
            skLineSegment(sketch, "E342", {"start": v(-44.7, -15.3) * mm, "end": v(-40.72, -15.3) * mm});
            skLineSegment(sketch, "E343", {"start": v(-40.72, -15.3) * mm, "end": v(-44.7, -19.28) * mm});
            skLineSegment(sketch, "E344", {"start": v(-44.7, -19.28) * mm, "end": v(-44.7, -15.3) * mm});
            skLineSegment(sketch, "E345", {"start": v(-40.3, -15.72) * mm, "end": v(-40.3, -19.7) * mm});
            skLineSegment(sketch, "E346", {"start": v(-40.3, -19.7) * mm, "end": v(-44.28, -19.7) * mm});
            skLineSegment(sketch, "E347", {"start": v(-44.28, -19.7) * mm, "end": v(-40.3, -15.72) * mm});
            skLineSegment(sketch, "E348", {"start": v(-30.3, -5.72) * mm, "end": v(-30.3, -9.7) * mm});
            skLineSegment(sketch, "E349", {"start": v(-30.3, -9.7) * mm, "end": v(-34.28, -9.7) * mm});
            skLineSegment(sketch, "E350", {"start": v(-34.28, -9.7) * mm, "end": v(-30.3, -5.72) * mm});
            skLineSegment(sketch, "E351", {"start": v(-10.3, 9.28) * mm, "end": v(-10.3, 5.3) * mm});
            skLineSegment(sketch, "E352", {"start": v(-10.3, 5.3) * mm, "end": v(-14.28, 5.3) * mm});
            skLineSegment(sketch, "E353", {"start": v(-14.28, 5.3) * mm, "end": v(-10.3, 9.28) * mm});
            skLineSegment(sketch, "E354", {"start": v(-9.7, 9.7) * mm, "end": v(-5.72, 9.7) * mm});
            skLineSegment(sketch, "E355", {"start": v(-5.72, 9.7) * mm, "end": v(-9.7, 5.72) * mm});
            skLineSegment(sketch, "E356", {"start": v(-9.7, 5.72) * mm, "end": v(-9.7, 9.7) * mm});
            skLineSegment(sketch, "E357", {"start": v(-5.3, 9.28) * mm, "end": v(-5.3, 5.3) * mm});
            skLineSegment(sketch, "E358", {"start": v(-5.3, 5.3) * mm, "end": v(-9.28, 5.3) * mm});
            skLineSegment(sketch, "E359", {"start": v(-9.28, 5.3) * mm, "end": v(-5.3, 9.28) * mm});
            skLineSegment(sketch, "E360", {"start": v(-0.3, 9.28) * mm, "end": v(-0.3, 5.3) * mm});
            skLineSegment(sketch, "E361", {"start": v(-0.3, 5.3) * mm, "end": v(-4.28, 5.3) * mm});
            skLineSegment(sketch, "E362", {"start": v(-4.28, 5.3) * mm, "end": v(-0.3, 9.28) * mm});
            skLineSegment(sketch, "E363", {"start": v(0.3, 9.7) * mm, "end": v(4.28, 9.7) * mm});
            skLineSegment(sketch, "E364", {"start": v(4.28, 9.7) * mm, "end": v(0.3, 5.72) * mm});
            skLineSegment(sketch, "E365", {"start": v(0.3, 5.72) * mm, "end": v(0.3, 9.7) * mm});
            skLineSegment(sketch, "E366", {"start": v(4.7, 9.28) * mm, "end": v(4.7, 5.3) * mm});
            skLineSegment(sketch, "E367", {"start": v(4.7, 5.3) * mm, "end": v(0.72, 5.3) * mm});
            skLineSegment(sketch, "E368", {"start": v(0.72, 5.3) * mm, "end": v(4.7, 9.28) * mm});
            skLineSegment(sketch, "E369", {"start": v(9.27, 4.7) * mm, "end": v(5.3, 0.72) * mm});
            skLineSegment(sketch, "E370", {"start": v(5.3, 0.72) * mm, "end": v(5.3, 4.7) * mm});
            skLineSegment(sketch, "E371", {"start": v(5.3, 4.7) * mm, "end": v(9.27, 4.7) * mm});
            skLineSegment(sketch, "E372", {"start": v(5.3, -10.3) * mm, "end": v(9.28, -10.3) * mm});
            skLineSegment(sketch, "E373", {"start": v(9.28, -10.3) * mm, "end": v(5.3, -14.28) * mm});
            skLineSegment(sketch, "E374", {"start": v(5.3, -14.28) * mm, "end": v(5.3, -10.3) * mm});
            skLineSegment(sketch, "E375", {"start": v(0.3, -24.28) * mm, "end": v(0.3, -20.3) * mm});
            skLineSegment(sketch, "E376", {"start": v(0.3, -20.3) * mm, "end": v(4.28, -20.3) * mm});
            skLineSegment(sketch, "E377", {"start": v(4.28, -20.3) * mm, "end": v(0.3, -24.28) * mm});
            skLineSegment(sketch, "E378", {"start": v(-4.7, -29.28) * mm, "end": v(-4.7, -25.3) * mm});
            skLineSegment(sketch, "E379", {"start": v(-4.7, -25.3) * mm, "end": v(-0.72, -25.3) * mm});
            skLineSegment(sketch, "E380", {"start": v(-0.72, -25.3) * mm, "end": v(-4.7, -29.28) * mm});
            skLineSegment(sketch, "E381", {"start": v(-9.7, -34.28) * mm, "end": v(-9.7, -30.3) * mm});
            skLineSegment(sketch, "E382", {"start": v(-9.7, -30.3) * mm, "end": v(-5.72, -30.3) * mm});
            skLineSegment(sketch, "E383", {"start": v(-5.72, -30.3) * mm, "end": v(-9.7, -34.28) * mm});
            skLineSegment(sketch, "E384", {"start": v(-14.7, -39.28) * mm, "end": v(-14.7, -35.3) * mm});
            skLineSegment(sketch, "E385", {"start": v(-14.7, -35.3) * mm, "end": v(-10.72, -35.3) * mm});
            skLineSegment(sketch, "E386", {"start": v(-10.72, -35.3) * mm, "end": v(-14.7, -39.28) * mm});
            skLineSegment(sketch, "E387", {"start": v(-15.3, -40.72) * mm, "end": v(-15.3, -44.7) * mm});
            skLineSegment(sketch, "E388", {"start": v(-15.3, -44.7) * mm, "end": v(-19.28, -44.7) * mm});
            skLineSegment(sketch, "E389", {"start": v(-19.28, -44.7) * mm, "end": v(-15.3, -40.72) * mm});
            skLineSegment(sketch, "E390", {"start": v(-14.7, -40.3) * mm, "end": v(-10.72, -40.3) * mm});
            skLineSegment(sketch, "E391", {"start": v(-10.72, -40.3) * mm, "end": v(-14.7, -44.28) * mm});
            skLineSegment(sketch, "E392", {"start": v(-14.7, -44.28) * mm, "end": v(-14.7, -40.3) * mm});
            skLineSegment(sketch, "E393", {"start": v(-10.3, -40.72) * mm, "end": v(-10.3, -44.7) * mm});
            skLineSegment(sketch, "E394", {"start": v(-10.3, -44.7) * mm, "end": v(-14.28, -44.7) * mm});
            skLineSegment(sketch, "E395", {"start": v(-14.28, -44.7) * mm, "end": v(-10.3, -40.72) * mm});
            skLineSegment(sketch, "E396", {"start": v(14.7, -15.72) * mm, "end": v(14.7, -19.7) * mm});
            skLineSegment(sketch, "E397", {"start": v(14.7, -19.7) * mm, "end": v(10.72, -19.7) * mm});
            skLineSegment(sketch, "E398", {"start": v(10.72, -19.7) * mm, "end": v(14.7, -15.72) * mm});
            skLineSegment(sketch, "E399", {"start": v(20.3, 9.7) * mm, "end": v(24.27, 9.7) * mm});
            skLineSegment(sketch, "E400", {"start": v(24.27, 9.7) * mm, "end": v(20.3, 5.72) * mm});
            skLineSegment(sketch, "E401", {"start": v(20.3, 5.72) * mm, "end": v(20.3, 9.7) * mm});
            skLineSegment(sketch, "E402", {"start": v(39.7, 20.3) * mm, "end": v(35.72, 20.3) * mm});
            skLineSegment(sketch, "E403", {"start": v(35.72, 20.3) * mm, "end": v(39.7, 24.28) * mm});
            skLineSegment(sketch, "E404", {"start": v(39.7, 24.28) * mm, "end": v(39.7, 20.3) * mm});
            skLineSegment(sketch, "E405", {"start": v(44.7, 34.28) * mm, "end": v(44.7, 30.3) * mm});
            skLineSegment(sketch, "E406", {"start": v(44.7, 30.3) * mm, "end": v(40.72, 30.3) * mm});
            skLineSegment(sketch, "E407", {"start": v(40.72, 30.3) * mm, "end": v(44.7, 34.28) * mm});
            skLineSegment(sketch, "E408", {"start": v(44.7, 39.28) * mm, "end": v(44.7, 35.3) * mm});
            skLineSegment(sketch, "E409", {"start": v(44.7, 35.3) * mm, "end": v(40.72, 35.3) * mm});
            skLineSegment(sketch, "E410", {"start": v(40.72, 35.3) * mm, "end": v(44.7, 39.28) * mm});
            skLineSegment(sketch, "E411", {"start": v(39.7, 34.28) * mm, "end": v(39.7, 30.3) * mm});
            skLineSegment(sketch, "E412", {"start": v(39.7, 30.3) * mm, "end": v(35.72, 30.3) * mm});
            skLineSegment(sketch, "E413", {"start": v(35.72, 30.3) * mm, "end": v(39.7, 34.28) * mm});
            skLineSegment(sketch, "E414", {"start": v(34.7, 29.28) * mm, "end": v(34.7, 25.3) * mm});
            skLineSegment(sketch, "E415", {"start": v(34.7, 25.3) * mm, "end": v(30.72, 25.3) * mm});
            skLineSegment(sketch, "E416", {"start": v(30.72, 25.3) * mm, "end": v(34.7, 29.28) * mm});
            skLineSegment(sketch, "E417", {"start": v(29.7, 24.28) * mm, "end": v(29.7, 20.3) * mm});
            skLineSegment(sketch, "E418", {"start": v(29.7, 20.3) * mm, "end": v(25.72, 20.3) * mm});
            skLineSegment(sketch, "E419", {"start": v(25.72, 20.3) * mm, "end": v(29.7, 24.28) * mm});
            skLineSegment(sketch, "E420", {"start": v(20.3, 25.72) * mm, "end": v(20.3, 29.7) * mm});
            skLineSegment(sketch, "E421", {"start": v(20.3, 29.7) * mm, "end": v(24.28, 29.7) * mm});
            skLineSegment(sketch, "E422", {"start": v(24.28, 29.7) * mm, "end": v(20.3, 25.72) * mm});
            skLineSegment(sketch, "E423", {"start": v(25.3, 30.72) * mm, "end": v(25.3, 34.7) * mm});
            skLineSegment(sketch, "E424", {"start": v(25.3, 34.7) * mm, "end": v(29.28, 34.7) * mm});
            skLineSegment(sketch, "E425", {"start": v(29.28, 34.7) * mm, "end": v(25.3, 30.72) * mm});
            skLineSegment(sketch, "E426", {"start": v(30.3, 35.72) * mm, "end": v(30.3, 39.7) * mm});
            skLineSegment(sketch, "E427", {"start": v(30.3, 39.7) * mm, "end": v(34.28, 39.7) * mm});
            skLineSegment(sketch, "E428", {"start": v(34.28, 39.7) * mm, "end": v(30.3, 35.72) * mm});
            skLineSegment(sketch, "E429", {"start": v(35.3, 40.72) * mm, "end": v(35.3, 44.7) * mm});
            skLineSegment(sketch, "E430", {"start": v(35.3, 44.7) * mm, "end": v(39.28, 44.7) * mm});
            skLineSegment(sketch, "E431", {"start": v(39.28, 44.7) * mm, "end": v(35.3, 40.72) * mm});
            skLineSegment(sketch, "E432", {"start": v(29.7, 44.28) * mm, "end": v(29.7, 40.3) * mm});
            skLineSegment(sketch, "E433", {"start": v(29.7, 40.3) * mm, "end": v(25.72, 40.3) * mm});
            skLineSegment(sketch, "E434", {"start": v(25.72, 40.3) * mm, "end": v(29.7, 44.28) * mm});
            skLineSegment(sketch, "E435", {"start": v(19.7, 39.28) * mm, "end": v(19.7, 35.3) * mm});
            skLineSegment(sketch, "E436", {"start": v(19.7, 35.3) * mm, "end": v(15.72, 35.3) * mm});
            skLineSegment(sketch, "E437", {"start": v(15.72, 35.3) * mm, "end": v(19.7, 39.28) * mm});
            skLineSegment(sketch, "E438", {"start": v(14.7, 30.3) * mm, "end": v(10.72, 30.3) * mm});
            skLineSegment(sketch, "E439", {"start": v(10.72, 30.3) * mm, "end": v(14.7, 34.28) * mm});
            skLineSegment(sketch, "E440", {"start": v(14.7, 34.28) * mm, "end": v(14.7, 30.3) * mm});
            skLineSegment(sketch, "E441", {"start": v(-0.3, 19.28) * mm, "end": v(-0.3, 15.3) * mm});
            skLineSegment(sketch, "E442", {"start": v(-0.3, 15.3) * mm, "end": v(-4.28, 15.3) * mm});
            skLineSegment(sketch, "E443", {"start": v(-4.28, 15.3) * mm, "end": v(-0.3, 19.28) * mm});
            skLineSegment(sketch, "E444", {"start": v(-20.3, 14.28) * mm, "end": v(-20.3, 10.3) * mm});
            skLineSegment(sketch, "E445", {"start": v(-20.3, 10.3) * mm, "end": v(-24.28, 10.3) * mm});
            skLineSegment(sketch, "E446", {"start": v(-24.28, 10.3) * mm, "end": v(-20.3, 14.28) * mm});
            skLineSegment(sketch, "E447", {"start": v(-25.3, 9.28) * mm, "end": v(-25.3, 5.3) * mm});
            skLineSegment(sketch, "E448", {"start": v(-25.3, 5.3) * mm, "end": v(-29.28, 5.3) * mm});
            skLineSegment(sketch, "E449", {"start": v(-29.28, 5.3) * mm, "end": v(-25.3, 9.28) * mm});
            skLineSegment(sketch, "E450", {"start": v(-30.3, 4.28) * mm, "end": v(-30.3, 0.3) * mm});
            skLineSegment(sketch, "E451", {"start": v(-30.3, 0.3) * mm, "end": v(-34.28, 0.3) * mm});
            skLineSegment(sketch, "E452", {"start": v(-34.28, 0.3) * mm, "end": v(-30.3, 4.28) * mm});
            skLineSegment(sketch, "E453", {"start": v(-35.3, -0.72) * mm, "end": v(-35.3, -4.7) * mm});
            skLineSegment(sketch, "E454", {"start": v(-35.3, -4.7) * mm, "end": v(-39.28, -4.7) * mm});
            skLineSegment(sketch, "E455", {"start": v(-39.28, -4.7) * mm, "end": v(-35.3, -0.72) * mm});
            skLineSegment(sketch, "E456", {"start": v(-40.3, -9.7) * mm, "end": v(-44.28, -9.7) * mm});
            skLineSegment(sketch, "E457", {"start": v(-44.28, -9.7) * mm, "end": v(-40.3, -5.72) * mm});
            skLineSegment(sketch, "E458", {"start": v(-40.3, -5.72) * mm, "end": v(-40.3, -9.7) * mm});
            skLineSegment(sketch, "E459", {"start": v(-39.7, -19.28) * mm, "end": v(-39.7, -15.3) * mm});
            skLineSegment(sketch, "E460", {"start": v(-39.7, -15.3) * mm, "end": v(-35.72, -15.3) * mm});
            skLineSegment(sketch, "E461", {"start": v(-35.72, -15.3) * mm, "end": v(-39.7, -19.28) * mm});
            skLineSegment(sketch, "E462", {"start": v(-34.7, -14.28) * mm, "end": v(-34.7, -10.3) * mm});
            skLineSegment(sketch, "E463", {"start": v(-34.7, -10.3) * mm, "end": v(-30.72, -10.3) * mm});
            skLineSegment(sketch, "E464", {"start": v(-30.72, -10.3) * mm, "end": v(-34.7, -14.28) * mm});
            skLineSegment(sketch, "E465", {"start": v(-29.7, -9.28) * mm, "end": v(-29.7, -5.3) * mm});
            skLineSegment(sketch, "E466", {"start": v(-29.7, -5.3) * mm, "end": v(-25.72, -5.3) * mm});
            skLineSegment(sketch, "E467", {"start": v(-25.72, -5.3) * mm, "end": v(-29.7, -9.28) * mm});
            skLineSegment(sketch, "E468", {"start": v(-24.7, -4.28) * mm, "end": v(-24.7, -0.3) * mm});
            skLineSegment(sketch, "E469", {"start": v(-24.7, -0.3) * mm, "end": v(-20.72, -0.3) * mm});
            skLineSegment(sketch, "E470", {"start": v(-20.72, -0.3) * mm, "end": v(-24.7, -4.28) * mm});
            skLineSegment(sketch, "E471", {"start": v(-19.7, 4.7) * mm, "end": v(-15.72, 4.7) * mm});
            skLineSegment(sketch, "E472", {"start": v(-15.72, 4.7) * mm, "end": v(-19.7, 0.72) * mm});
            skLineSegment(sketch, "E473", {"start": v(-19.7, 0.72) * mm, "end": v(-19.7, 4.7) * mm});
            skLineSegment(sketch, "E474", {"start": v(4.7, -15.72) * mm, "end": v(4.7, -19.7) * mm});
            skLineSegment(sketch, "E475", {"start": v(4.7, -19.7) * mm, "end": v(0.72, -19.7) * mm});
            skLineSegment(sketch, "E476", {"start": v(0.72, -19.7) * mm, "end": v(4.7, -15.72) * mm});
            skLineSegment(sketch, "E477", {"start": v(-0.3, -20.72) * mm, "end": v(-0.3, -24.7) * mm});
            skLineSegment(sketch, "E478", {"start": v(-0.3, -24.7) * mm, "end": v(-4.28, -24.7) * mm});
            skLineSegment(sketch, "E479", {"start": v(-4.28, -24.7) * mm, "end": v(-0.3, -20.72) * mm});
            skLineSegment(sketch, "E480", {"start": v(-5.3, -25.72) * mm, "end": v(-5.3, -29.7) * mm});
            skLineSegment(sketch, "E481", {"start": v(-5.3, -29.7) * mm, "end": v(-9.28, -29.7) * mm});
            skLineSegment(sketch, "E482", {"start": v(-9.28, -29.7) * mm, "end": v(-5.3, -25.72) * mm});
            skLineSegment(sketch, "E483", {"start": v(-10.3, -30.72) * mm, "end": v(-10.3, -34.7) * mm});
            skLineSegment(sketch, "E484", {"start": v(-10.3, -34.7) * mm, "end": v(-14.28, -34.7) * mm});
            skLineSegment(sketch, "E485", {"start": v(-14.28, -34.7) * mm, "end": v(-10.3, -30.72) * mm});
            skLineSegment(sketch, "E486", {"start": v(-15.3, -39.7) * mm, "end": v(-19.28, -39.7) * mm});
            skLineSegment(sketch, "E487", {"start": v(-19.28, -39.7) * mm, "end": v(-15.3, -35.72) * mm});
            skLineSegment(sketch, "E488", {"start": v(-15.3, -35.72) * mm, "end": v(-15.3, -39.7) * mm});
            skLineSegment(sketch, "E489", {"start": v(-9.7, -44.28) * mm, "end": v(-9.7, -40.3) * mm});
            skLineSegment(sketch, "E490", {"start": v(-9.7, -40.3) * mm, "end": v(-5.72, -40.3) * mm});
            skLineSegment(sketch, "E491", {"start": v(-5.72, -40.3) * mm, "end": v(-9.7, -44.28) * mm});
            skLineSegment(sketch, "E492", {"start": v(-4.7, -39.28) * mm, "end": v(-4.7, -35.3) * mm});
            skLineSegment(sketch, "E493", {"start": v(-4.7, -35.3) * mm, "end": v(-0.72, -35.3) * mm});
            skLineSegment(sketch, "E494", {"start": v(-0.72, -35.3) * mm, "end": v(-4.7, -39.28) * mm});
            skLineSegment(sketch, "E495", {"start": v(0.3, -34.28) * mm, "end": v(0.3, -30.3) * mm});
            skLineSegment(sketch, "E496", {"start": v(0.3, -30.3) * mm, "end": v(4.28, -30.3) * mm});
            skLineSegment(sketch, "E497", {"start": v(4.28, -30.3) * mm, "end": v(0.3, -34.28) * mm});
            skLineSegment(sketch, "E498", {"start": v(5.3, -29.28) * mm, "end": v(5.3, -25.3) * mm});
            skLineSegment(sketch, "E499", {"start": v(5.3, -25.3) * mm, "end": v(9.28, -25.3) * mm});
            skLineSegment(sketch, "E500", {"start": v(9.28, -25.3) * mm, "end": v(5.3, -29.28) * mm});
            skLineSegment(sketch, "E501", {"start": v(10.3, -24.28) * mm, "end": v(10.3, -20.3) * mm});
            skLineSegment(sketch, "E502", {"start": v(10.3, -20.3) * mm, "end": v(14.28, -20.3) * mm});
            skLineSegment(sketch, "E503", {"start": v(14.28, -20.3) * mm, "end": v(10.3, -24.28) * mm});
            skLineSegment(sketch, "E504", {"start": v(15.3, -4.28) * mm, "end": v(15.3, -0.3) * mm});
            skLineSegment(sketch, "E505", {"start": v(15.3, -0.3) * mm, "end": v(19.28, -0.3) * mm});
            skLineSegment(sketch, "E506", {"start": v(19.28, -0.3) * mm, "end": v(15.3, -4.28) * mm});
            skLineSegment(sketch, "E507", {"start": v(20.72, 5.3) * mm, "end": v(24.7, 9.28) * mm});
            skLineSegment(sketch, "E508", {"start": v(24.7, 9.28) * mm, "end": v(24.7, 5.3) * mm});
            skLineSegment(sketch, "E509", {"start": v(24.7, 5.3) * mm, "end": v(20.72, 5.3) * mm});
            skLineSegment(sketch, "E510", {"start": v(25.3, 5.72) * mm, "end": v(25.3, 9.7) * mm});
            skLineSegment(sketch, "E511", {"start": v(25.3, 9.7) * mm, "end": v(29.28, 9.7) * mm});
            skLineSegment(sketch, "E512", {"start": v(29.28, 9.7) * mm, "end": v(25.3, 5.72) * mm});
            skLineSegment(sketch, "E513", {"start": v(30.3, 10.72) * mm, "end": v(30.3, 14.7) * mm});
            skLineSegment(sketch, "E514", {"start": v(30.3, 14.7) * mm, "end": v(34.28, 14.7) * mm});
            skLineSegment(sketch, "E515", {"start": v(34.28, 14.7) * mm, "end": v(30.3, 10.72) * mm});
            skLineSegment(sketch, "E516", {"start": v(35.3, 15.72) * mm, "end": v(35.3, 19.7) * mm});
            skLineSegment(sketch, "E517", {"start": v(35.3, 19.7) * mm, "end": v(39.28, 19.7) * mm});
            skLineSegment(sketch, "E518", {"start": v(39.28, 19.7) * mm, "end": v(35.3, 15.72) * mm});
            skLineSegment(sketch, "E519", {"start": v(40.3, 25.72) * mm, "end": v(40.3, 29.7) * mm});
            skLineSegment(sketch, "E520", {"start": v(40.3, 29.7) * mm, "end": v(44.28, 29.7) * mm});
            skLineSegment(sketch, "E521", {"start": v(44.28, 29.7) * mm, "end": v(40.3, 25.72) * mm});
            skLineSegment(sketch, "E522", {"start": v(-20.3, -45.3) * mm, "end": v(-20.3, -39.88) * mm});
            skLineSegment(sketch, "E523", {"start": v(-20.3, -39.88) * mm, "end": v(4.7, -14.88) * mm});
            skLineSegment(sketch, "E524", {"start": v(4.7, -14.88) * mm, "end": v(4.7, 4.7) * mm});
            skLineSegment(sketch, "E525", {"start": v(4.7, 4.7) * mm, "end": v(-14.88, 4.7) * mm});
            skLineSegment(sketch, "E526", {"start": v(-14.88, 4.7) * mm, "end": v(-39.88, -20.3) * mm});
            skLineSegment(sketch, "E527", {"start": v(-39.88, -20.3) * mm, "end": v(-45.3, -20.3) * mm});
            skLineSegment(sketch, "E528", {"start": v(-45.3, -20.3) * mm, "end": v(-45.3, -9.88) * mm});
            skLineSegment(sketch, "E529", {"start": v(-45.3, -9.88) * mm, "end": v(-20.12, 15.3) * mm});
            skLineSegment(sketch, "E530", {"start": v(-20.12, 15.3) * mm, "end": v(-5.12, 15.3) * mm});
            skLineSegment(sketch, "E531", {"start": v(-5.12, 15.3) * mm, "end": v(-0.12, 20.3) * mm});
            skLineSegment(sketch, "E532", {"start": v(-0.12, 20.3) * mm, "end": v(4.7, 20.3) * mm});
            skLineSegment(sketch, "E533", {"start": v(4.7, 20.3) * mm, "end": v(4.7, 25.12) * mm});
            skLineSegment(sketch, "E534", {"start": v(4.7, 25.12) * mm, "end": v(19.88, 40.3) * mm});
            skLineSegment(sketch, "E535", {"start": v(19.88, 40.3) * mm, "end": v(24.88, 40.3) * mm});
            skLineSegment(sketch, "E536", {"start": v(24.88, 40.3) * mm, "end": v(29.88, 45.3) * mm});
            skLineSegment(sketch, "E537", {"start": v(29.88, 45.3) * mm, "end": v(40.72, 45.3) * mm});
            skLineSegment(sketch, "E538", {"start": v(40.72, 45.3) * mm, "end": v(20.3, 24.88) * mm});
            skLineSegment(sketch, "E539", {"start": v(20.3, 24.88) * mm, "end": v(20.3, 20.3) * mm});
            skLineSegment(sketch, "E540", {"start": v(20.3, 20.3) * mm, "end": v(24.88, 20.3) * mm});
            skLineSegment(sketch, "E541", {"start": v(24.88, 20.3) * mm, "end": v(45.3, 40.72) * mm});
            skLineSegment(sketch, "E542", {"start": v(45.3, 40.72) * mm, "end": v(45.3, 29.88) * mm});
            skLineSegment(sketch, "E543", {"start": v(45.3, 29.88) * mm, "end": v(40.3, 24.88) * mm});
            skLineSegment(sketch, "E544", {"start": v(40.3, 24.88) * mm, "end": v(40.3, 19.88) * mm});
            skLineSegment(sketch, "E545", {"start": v(40.3, 19.88) * mm, "end": v(25.12, 4.7) * mm});
            skLineSegment(sketch, "E546", {"start": v(25.12, 4.7) * mm, "end": v(20.3, 4.7) * mm});
            skLineSegment(sketch, "E547", {"start": v(20.3, 4.7) * mm, "end": v(20.3, -0.12) * mm});
            skLineSegment(sketch, "E548", {"start": v(20.3, -0.12) * mm, "end": v(15.3, -5.12) * mm});
            skLineSegment(sketch, "E549", {"start": v(15.3, -5.12) * mm, "end": v(15.3, -20.12) * mm});
            skLineSegment(sketch, "E550", {"start": v(15.3, -20.12) * mm, "end": v(-9.88, -45.3) * mm});
            skLineSegment(sketch, "E551", {"start": v(-9.88, -45.3) * mm, "end": v(-20.3, -45.3) * mm});
            skSolve(sketch);
        }
        {
            var Q0;
            Q0=makeQuery(id+"F0.imprint","IMPRINT",FACE,{"disambiguationData":[TD([[makeQuery(id+"F0.imprint","IMPRINT",EDGE,{"derivedFrom":sQuery(id+"F0.wireOp",EDGE,"E0")}),1.0]])]});
            extrude(context, id + "F1", {"entities" : qUnion([Q0]), "depth" : 5 * mm});
        }
    });
